# Revit family: OC-FLANGE_LF_DN250_PN16_RFA_2018
name_source: partatom
category: Pipe Accessories
revit_build: Autodesk Revit LT 2018 (Build: 20180329_1100(x64)
units: mm (PartAtom-declared; Revit-internal decimal feet)

## family parameters
Always vertical = Yes
Cut with Voids When Loaded = No
Part Type = Valve - Breaks Into
Round Connector Dimension = Use Diameter
Shared = No
Work Plane-Based = No

## types (2) — shared parameters
A3WP = 112 mm  [stored 0.367454 ft]
ACT2H = 311 mm  [stored 1.02034 ft]
ACT2L = 230 mm  [stored 0.754593 ft]
ACT3L = 93 mm
ACT3W = 167 mm  [stored 0.5479 ft]
AL2 = 156 mm  [stored 0.511811 ft]
CAT0 = Yes
DD = Yes
Description = Tlakově nezávislý 2-cestný regulační vyvažovací ventil (PICV)
H3 = 15 mm  [stored 0.0492126 ft]
L2D = 230 mm  [stored 0.754593 ft]
L2D_Min = 30 mm  [stored 0.0984252 ft]
MC Pressure Drop Maximum Value = 0.0 Pa
MC Pressure Drop Minimum Value = 0.0 Pa
MC Use Limits From Balancing Method = No
Manufacturer = Hydronic Systems Prague s.r.o.
QmdConnectorList = 301;D;302;D
Type Comments = Přírubový; PN16; 0~110°C, s měřením
URL = www.hydronic.cz
W2D = 50 mm  [stored 0.164042 ft]
magiPartTypeId = 304
magiProductFamilyId = f0b264c0d7504b12868dd3b486e32a
zero-valued in all types: MC Throttling Maximum Value, MC Throttling Minimum Value

## per-type parameters (varying)
| type | D | DF2 | H | H1 | H2 | H4 | H6 | L2 | L3 | L4 | LF | LF2 | LF__ve | MC Product Code | R1 | R3 | R4 | magiProductId |
| Optima Compact Flange PN16 DN250 LF | 250 mm | 222 mm  [stored 0.728346 ft] | 1094 mm  [stored 3.58924 ft] | 444 mm  [stored 1.45669 ft] | 244 mm | 67 mm | 339 mm | 365 mm  [stored 1.19751 ft] | 613 mm | 343 mm | 58 mm | 29 mm | -58 mm | 53-1207 (DN250 LF; 48mm; pohon min 2500N; Qmin-dpmin 190000l/h-10.0kPa; Qmax-dpmin 475000l/h-35.0kPa; dpmax 800kPa) | 275 mm | 115 mm | 192 mm | 4254bd6dcc3e44f98f38d0e788b611 |
| Optima Compact Flange PN16 DN300 LF | 300 mm | 260 mm  [stored 0.853018 ft] | 1132 mm  [stored 3.71391 ft] | 520 mm  [stored 1.70604 ft] | 286 mm  [stored 0.93832 ft] | 78 mm  [stored 0.255906 ft] | 290 mm  [stored 0.951444 ft] | 425 mm  [stored 1.39436 ft] | 714 mm  [stored 2.34252 ft] | 400 mm  [stored 1.31234 ft] | 68 mm  [stored 0.223097 ft] | 34 mm  [stored 0.111549 ft] | -68 mm  [stored -0.223097 ft] | 53-1208 (DN300 LF; 48mm; pohon min 2500N; Qmin-dpmin 190000l/h-10.0kPa; Qmax-dpmin 475000l/h-35.0kPa; dpmax 800kPa) | 360 mm | 135 mm  [stored 0.442913 ft] | 252 mm | ecb81ef8531940baa5b8b8db4f8dfa |

note: [stored X ft] marks values corroborated as IEEE doubles in the binary element streams (Revit-internal decimal feet)

## geometry (parser evidence)
native form markers: Sweep x1
no freeform markers — native parametric forms only
